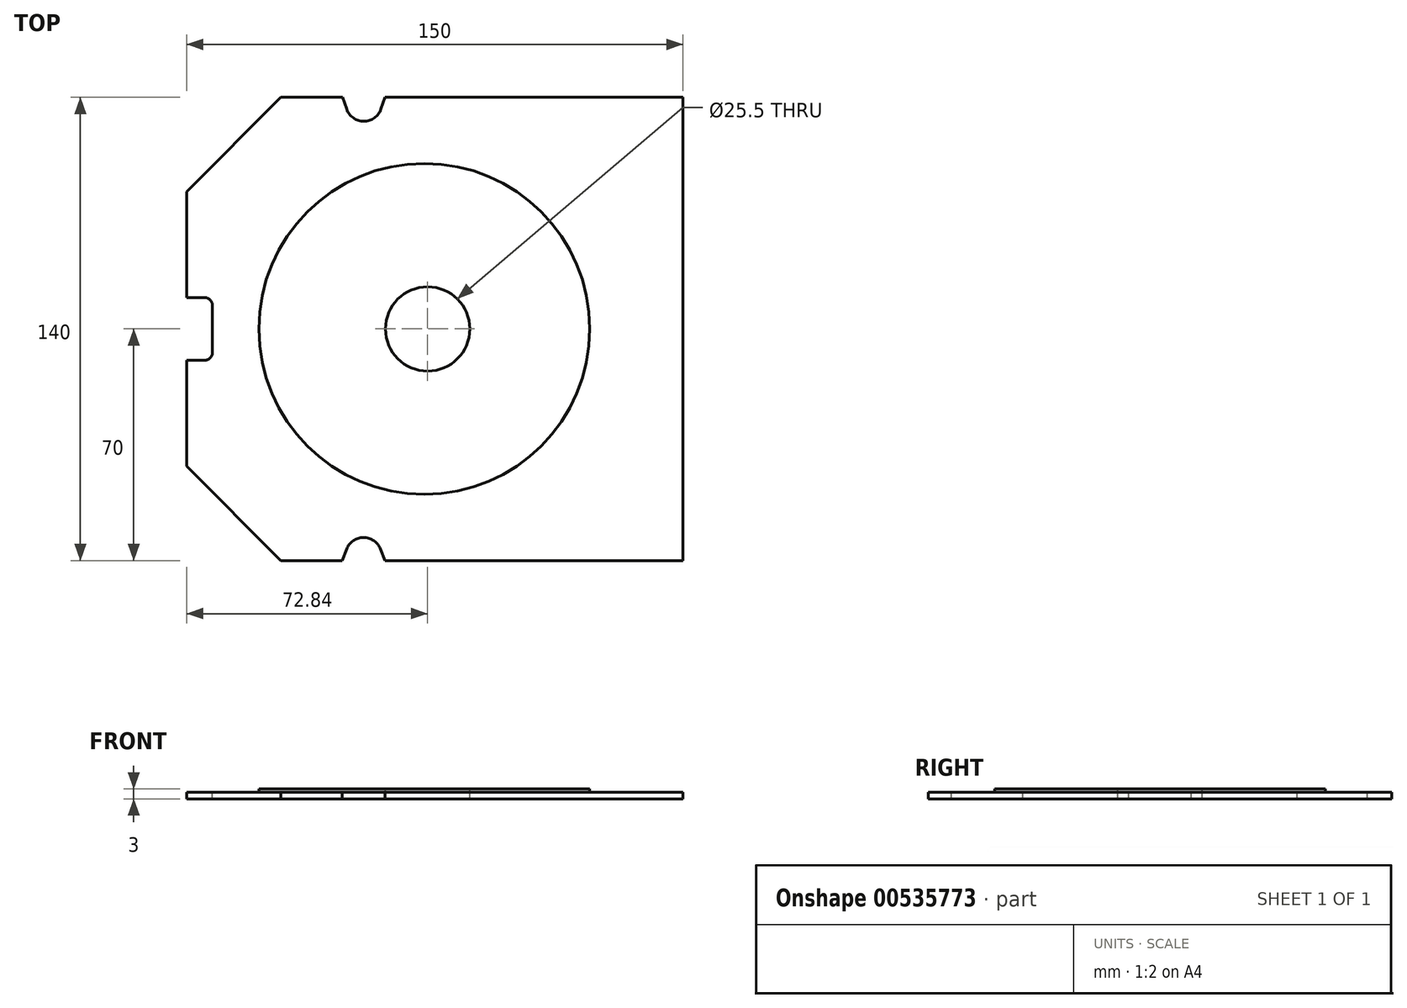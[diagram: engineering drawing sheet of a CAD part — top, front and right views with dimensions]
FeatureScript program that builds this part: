
annotation { "Feature Type Name" : "Feature", "Feature Type Description" : "" }
export const myFeature = defineFeature(function(context is Context, id is Id, definition is map)
    precondition{}
    {
        {
            var Q0;
            Q0=qCreatedBy(makeId("Top.planeOp"),FACE);
            var sketch = newSketch(context, id + "F0", { "sketchPlane" : qUnion([Q0])});
            skLineSegment(sketch, "E0.bottom", {"start": v(75, -70) * mm, "end": v(-75, -70) * mm});
            skLineSegment(sketch, "E0.top", {"start": v(75, 70) * mm, "end": v(-75, 70) * mm});
            skLineSegment(sketch, "E0.left", {"start": v(75, -70) * mm, "end": v(75, 70) * mm});
            skLineSegment(sketch, "E0.right", {"start": v(-75, -70) * mm, "end": v(-75, 70) * mm});
            skPoint(sketch, "E0.middle", {"position": v(0, 0) * mm});
            skSolve(sketch);
        }
        {
            var Q0;
            Q0=qSketchRegion(id+"F0",true);
            extrude(context, id + "F1", {"entities" : qUnion([Q0]), "depth" : 2 * mm, "offsetDistance" : 25 * mm});
        }
        {
            var Q0;
            Q0=makeQuery(id+"F1.opExtrude","CAP_FACE",FACE,{"disambiguationData":[OSD([sQuery(id+"F0.wireOp",EDGE,"E0.bottom"),sQuery(id+"F0.wireOp",EDGE,"E0.top"),sQuery(id+"F0.wireOp",EDGE,"E0.left"),sQuery(id+"F0.wireOp",EDGE,"E0.right")])],"isStart":false});
            var sketch = newSketch(context, id + "F2", { "sketchPlane" : qUnion([Q0])});
            skLineSegment(sketch, "E1", {"start": v(-75, 41.5) * mm, "end": v(-46.5, 70) * mm});
            skLineSegment(sketch, "E2", {"start": v(-75, -41.5) * mm, "end": v(-46.5, -70) * mm});
            skSolve(sketch);
        }
        {
            var Q0;
            Q0=qSketchRegion(id+"F2",true);
            var Q1;
            {var subQ0=sQuery(id+"F2.wireOp",EDGE,"E1");Q1=makeQuery(id+"F2.imprint","IMPRINT",FACE,{"disambiguationData":[TD([[makeQuery(id+"F2.imprint","IMPRINT",EDGE,{"derivedFrom":subQ0}),1.0]])]});}
            var Q2;
            {var subQ0=sQuery(id+"F2.wireOp",EDGE,"E2");Q2=makeQuery(id+"F2.imprint","IMPRINT",FACE,{"disambiguationData":[TD([[makeQuery(id+"F2.imprint","IMPRINT",EDGE,{"derivedFrom":subQ0}),-1.0]])]});}
            extrude(context, id + "F3", {"entities" : qUnion([Q0, Q1, Q2]), "operationType" : NewBodyOperationType.REMOVE, "endBound" : BoundingType.THROUGH_ALL, "oppositeDirection" : true, "depth" : 25 * mm, "offsetDistance" : 25 * mm});
        }
        {
            var Q0;
            Q0=makeQuery(id+"F1.opExtrude","CAP_FACE",FACE,{"disambiguationData":[OSD([sQuery(id+"F0.wireOp",EDGE,"E0.bottom"),sQuery(id+"F0.wireOp",EDGE,"E0.top"),sQuery(id+"F0.wireOp",EDGE,"E0.left"),sQuery(id+"F0.wireOp",EDGE,"E0.right")])],"isStart":false});
            var sketch = newSketch(context, id + "F4", { "sketchPlane" : qUnion([Q0])});
            skLineSegment(sketch, "E3", {"start": v(-75, 9.5) * mm, "end": v(-69.68, 9.5) * mm});
            skLineSegment(sketch, "E4", {"start": v(-67.18, 7) * mm, "end": v(-67.18, -7) * mm});
            skArc(sketch, "E5", {"start": v(-67.18, 7) * mm, "mid": v(-67.91, 8.77) * mm, "end": v(-69.68, 9.5) * mm});
            skLineSegment(sketch, "E6", {"start": v(-75, -9.5) * mm, "end": v(-69.68, -9.5) * mm});
            skArc(sketch, "E7", {"start": v(-69.68, -9.5) * mm, "mid": v(-67.91, -8.77) * mm, "end": v(-67.18, -7) * mm});
            skSolve(sketch);
        }
        {
            var Q0;
            Q0=qSketchRegion(id+"F4",true);
            var Q1;
            {var subQ1=sQuery(id+"F4.wireOp",EDGE,"E3");Q1=makeQuery(id+"F4.imprint","IMPRINT",FACE,{"disambiguationData":[TD([[makeQuery(id+"F4.imprint","IMPRINT",EDGE,{"derivedFrom":subQ1}),-1.0]])]});}
            extrude(context, id + "F5", {"entities" : qUnion([Q0, Q1]), "operationType" : NewBodyOperationType.REMOVE, "endBound" : BoundingType.THROUGH_ALL, "oppositeDirection" : true, "depth" : 25 * mm, "offsetDistance" : 25 * mm});
        }
        {
            var Q0;
            Q0=makeQuery(id+"F1.opExtrude","CAP_FACE",FACE,{"disambiguationData":[OSD([sQuery(id+"F0.wireOp",EDGE,"E0.bottom"),sQuery(id+"F0.wireOp",EDGE,"E0.top"),sQuery(id+"F0.wireOp",EDGE,"E0.left"),sQuery(id+"F0.wireOp",EDGE,"E0.right")])],"isStart":false});
            var sketch = newSketch(context, id + "F6", { "sketchPlane" : qUnion([Q0])});
            skArc(sketch, "E8", {"start": v(-26.63, 66.43) * mm, "mid": v(-21.44, 62.74) * mm, "end": v(-16.24, 66.43) * mm});
            skArc(sketch, "E9", {"start": v(-16.42, -66.5) * mm, "mid": v(-21.52, -63.06) * mm, "end": v(-26.61, -66.5) * mm});
            skLineSegment(sketch, "E10", {"start": v(-27.88, 70) * mm, "end": v(-26.63, 66.43) * mm});
            skLineSegment(sketch, "E11", {"start": v(-15, 70) * mm, "end": v(-16.24, 66.43) * mm});
            skLineSegment(sketch, "E12", {"start": v(-26.61, -66.5) * mm, "end": v(-28.03, -70) * mm});
            skLineSegment(sketch, "E13", {"start": v(-16.42, -66.5) * mm, "end": v(-15, -70) * mm});
            skSolve(sketch);
        }
        {
            var Q0;
            Q0=qSketchRegion(id+"F6",true);
            var Q1;
            Q1=makeQuery(id+"F6.imprint","IMPRINT",FACE,{"disambiguationData":[TD([[makeQuery(id+"F6.imprint","IMPRINT",EDGE,{"derivedFrom":sQuery(id+"F6.wireOp",EDGE,"E9")}),1.0]])]});
            var Q2;
            Q2=makeQuery(id+"F6.imprint","IMPRINT",FACE,{"disambiguationData":[TD([[makeQuery(id+"F6.imprint","IMPRINT",EDGE,{"derivedFrom":sQuery(id+"F6.wireOp",EDGE,"E8")}),1.0]])]});
            extrude(context, id + "F7", {"entities" : qUnion([Q0, Q1, Q2]), "operationType" : NewBodyOperationType.REMOVE, "endBound" : BoundingType.THROUGH_ALL, "oppositeDirection" : true, "depth" : 25 * mm, "offsetDistance" : 25 * mm});
        }
        {
            var Q0;
            Q0=makeQuery(id+"F1.opExtrude","CAP_FACE",FACE,{"disambiguationData":[OSD([sQuery(id+"F0.wireOp",EDGE,"E0.bottom"),sQuery(id+"F0.wireOp",EDGE,"E0.top"),sQuery(id+"F0.wireOp",EDGE,"E0.left"),sQuery(id+"F0.wireOp",EDGE,"E0.right")])],"isStart":false});
            var sketch = newSketch(context, id + "F8", { "sketchPlane" : qUnion([Q0])});
            skCircle(sketch, "E14", {"center": v(-3.16, 0) * mm, "radius": 50 * mm});
            skPoint(sketch, "E14.first.point", {"position": v(-36.36, 37.39) * mm});
            skPoint(sketch, "E14.second.point", {"position": v(32.35, -35.2) * mm});
            skPoint(sketch, "E14.third.point", {"position": v(42.82, 19.64) * mm});
            skSolve(sketch);
        }
        {
            var Q0;
            Q0=qSketchRegion(id+"F8",true);
            extrude(context, id + "F9", {"entities" : qUnion([Q0]), "operationType" : NewBodyOperationType.ADD, "depth" : 1 * mm, "offsetDistance" : 25 * mm});
        }
        {
            var Q0;
            Q0=makeQuery(id+"F9.opExtrude","CAP_FACE",FACE,{"disambiguationData":[OSD([sQuery(id+"F8.wireOp",EDGE,"E14")])],"isStart":false});
            var sketch = newSketch(context, id + "F10", { "sketchPlane" : qUnion([Q0])});
            skCircle(sketch, "E15", {"center": v(-2.16, 0) * mm, "radius": 12.75 * mm});
            skPoint(sketch, "E15.first.point", {"position": v(-14.91, 0) * mm});
            skPoint(sketch, "E15.second.point", {"position": v(10.59, 0) * mm});
            skPoint(sketch, "E15.third.point", {"position": v(-11.86, -8.27) * mm});
            skSolve(sketch);
        }
        {
            var Q0;
            Q0=makeQuery(id+"F10.imprint","IMPRINT",FACE,{"disambiguationData":[TD([[makeQuery(id+"F10.imprint","IMPRINT",EDGE,{"derivedFrom":sQuery(id+"F10.wireOp",EDGE,"E15")}),1.0]])]});
            extrude(context, id + "F11", {"entities" : qUnion([Q0]), "operationType" : NewBodyOperationType.REMOVE, "oppositeDirection" : true, "depth" : 25 * mm, "offsetDistance" : 25 * mm});
        }
    });
